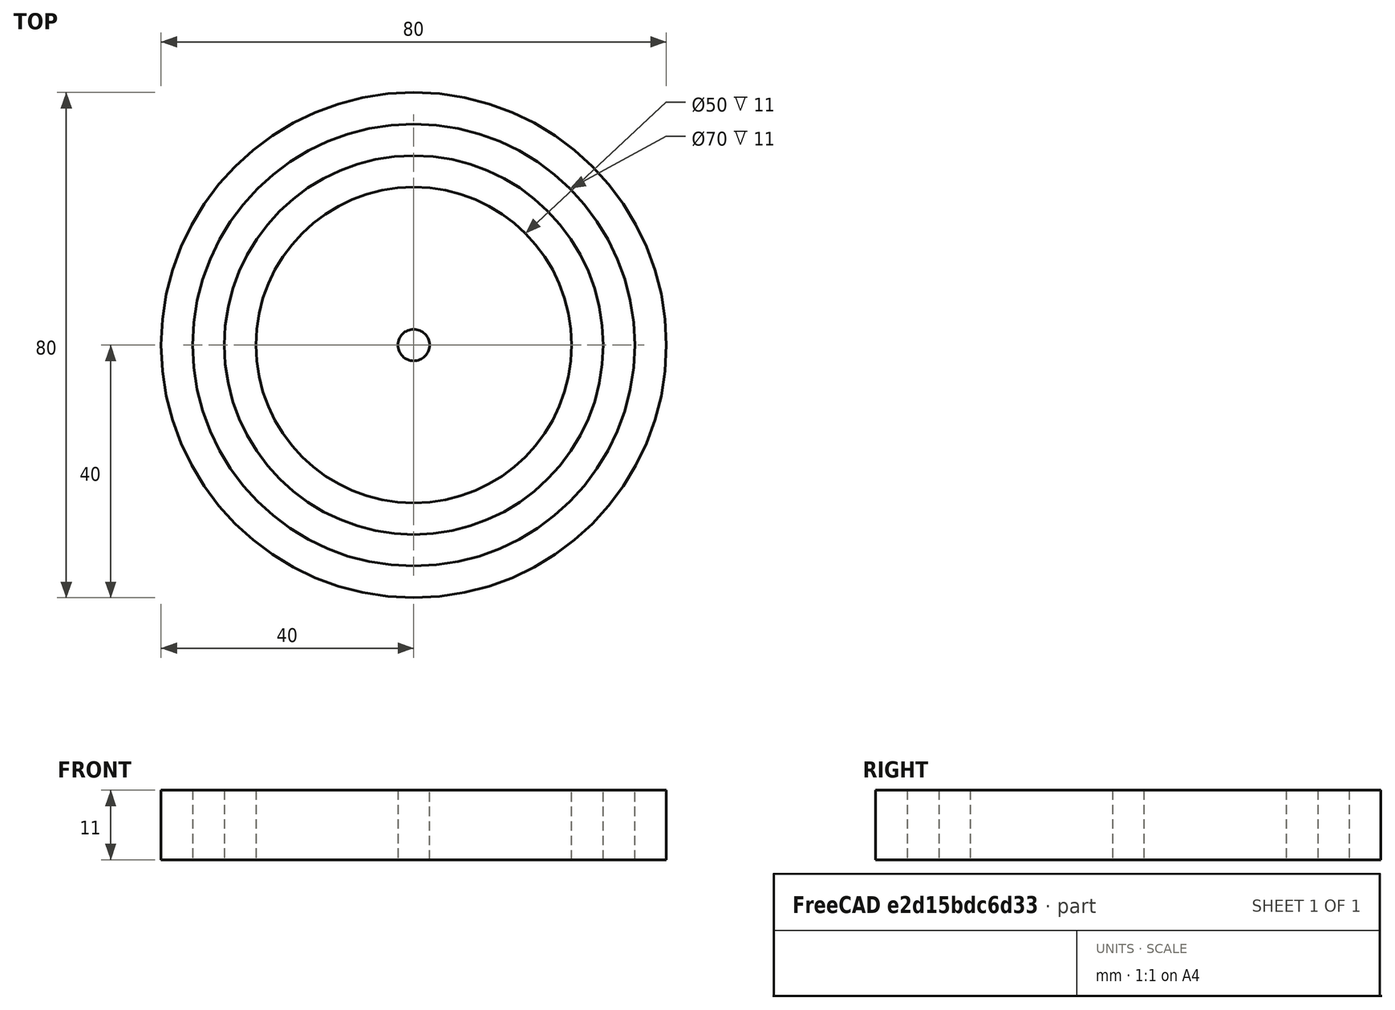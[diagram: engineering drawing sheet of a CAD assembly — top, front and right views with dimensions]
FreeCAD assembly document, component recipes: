
FREECAD ASSEMBLY — COMPONENT RECIPES ("Assambly_bearing_50x80x11")

This assembly document has 4 components, labeled P0..P3 below (a component is one placed body or linked part). 3 of them carry a construction recipe — the FreeCAD feature program that regenerates the part from scratch, quoted from this document or its linked companion documents; the rest are supplied as boundary geometry only. No exploded tour is included for this assembly.
COMPONENT P0 — geometry summary ("Assembly"; no construction recipe available for this part):
  bounding box: 80.0 x 80.0 x 11.0 mm
  tessellated surface: 208 triangles
  volume: 1188571428571428608091837590807025526931679251701097734487443175340447316937393037983811611623744864256 mm^3 (1688311688311688562448860555482270785700193953117129279461272140759222794130520652251307026134597632% of its bounding box)
  symmetry: 2-fold rotationally symmetric about the x axis; mirror-symmetric across its x mid-plane, z mid-plane
COMPONENT P1 — recipe-attached ("Body_ring_in", modeled in this document).
Construction recipe (the document's own serialized feature program — sketch geometry with constraints, then the solid features built on it; lengths are millimeters unless a unit is written):

FEATURE [Sketcher::SketchObject] Sketch002
  FullyConstrained = true
  MapMode = 5
  Support = -> [XY_Plane003]
  sketch-geometry (2):
    g0: Circle CenterX=0 CenterY=0 CenterZ=0 NormalX=0 NormalY=0 NormalZ=1 AngleXU=0 Radius=30
    g1: Circle CenterX=0 CenterY=0 CenterZ=0 NormalX=0 NormalY=0 NormalZ=1 AngleXU=0 Radius=25
  constraints (4):
    c: Coincident(g1,g0)
    c: Diameter(g1) = 50
    c: Diameter(g0) = 60
    c: Coincident(g0,g-1)
FEATURE [PartDesign::Pad] Pad001
  Direction = (1,1,1)
  Length = 11
  Length2 = 100
  Profile = -> Sketch002
  Type = 0
FEATURE [PartDesign::CoordinateSystem] LCS_Ring_in
  AttacherType = Attacher::AttachEngine3D
  MapMode = 11
  Placement = pos=(0,0,11) rot=(0,0,1;1.5708rad)
  Support = -> [Pad001]
FEATURE [PartDesign::Body] Body001  label="Body_ring_in"
  Group = -> [Sketch002,Pad001,LCS_Ring_in]
  Origin = -> Origin002
  Tip = -> Pad001
COMPONENT P2 — recipe-attached ("Body_roller", modeled in this document).
Construction recipe (the document's own serialized feature program — sketch geometry with constraints, then the solid features built on it; lengths are millimeters unless a unit is written):

FEATURE [Sketcher::SketchObject] Sketch003
  FullyConstrained = true
  MapMode = 5
  Support = -> [XY_Plane004]
  sketch-geometry (1):
    g0: Circle CenterX=0 CenterY=0 CenterZ=0 NormalX=0 NormalY=0 NormalZ=1 AngleXU=0 Radius=2.5
  constraints (2):
    c: Diameter(g0) = 5
    c: Coincident(g0,g-1)
FEATURE [PartDesign::Pad] Pad002
  Direction = (1,1,1)
  Length = 11
  Length2 = 100
  Profile = -> Sketch003
  Type = 0
FEATURE [PartDesign::CoordinateSystem] LCS_Roller
  AttacherType = Attacher::AttachEngine3D
  MapMode = 11
  Placement = pos=(0,0,11) rot=(0,0,1;1.5708rad)
  Support = -> [Pad002]
FEATURE [PartDesign::Body] Body002  label="Body_roller"
  Group = -> [Sketch003,Pad002,LCS_Roller]
  Origin = -> Origin003
  Tip = -> Pad002
COMPONENT P3 — recipe-attached ("Body_ring_out", modeled in this document).
Construction recipe (the document's own serialized feature program — sketch geometry with constraints, then the solid features built on it; lengths are millimeters unless a unit is written):

FEATURE [Sketcher::SketchObject] Sketch004
  FullyConstrained = true
  MapMode = 5
  Support = -> [XY_Plane005]
  sketch-geometry (2):
    g0: Circle CenterX=0 CenterY=0 CenterZ=0 NormalX=0 NormalY=0 NormalZ=1 AngleXU=0 Radius=35
    g1: Circle CenterX=0 CenterY=0 CenterZ=0 NormalX=0 NormalY=0 NormalZ=1 AngleXU=0 Radius=40
  constraints (4):
    c: Coincident(g1,g0)
    c: Diameter(g1) = 80
    c: Diameter(g0) = 70
    c: Coincident(g0,g-1)
FEATURE [PartDesign::Pad] Pad003
  Direction = (1,1,1)
  Length = 11
  Length2 = 100
  Profile = -> Sketch004
  Type = 0
FEATURE [PartDesign::CoordinateSystem] LCS_Ring_out
  AttacherType = Attacher::AttachEngine3D
  MapMode = 11
  Placement = pos=(0,0,11) rot=(0,0,1;1.5708rad)
  Support = -> [Pad003]
FEATURE [PartDesign::Body] Body003  label="Body_ring_out"
  Group = -> [Sketch004,Pad003,LCS_Ring_out]
  Origin = -> Origin004
  Tip = -> Pad003
PROVENANCE & LICENSES
A FreeCAD (.FCStd) document from a public repository crawl; recipes are the document's own serialized feature recipes (and, for linked parts, companion documents' recipes).
License: as declared in the source repository (recorded in the dataset sidecar).
